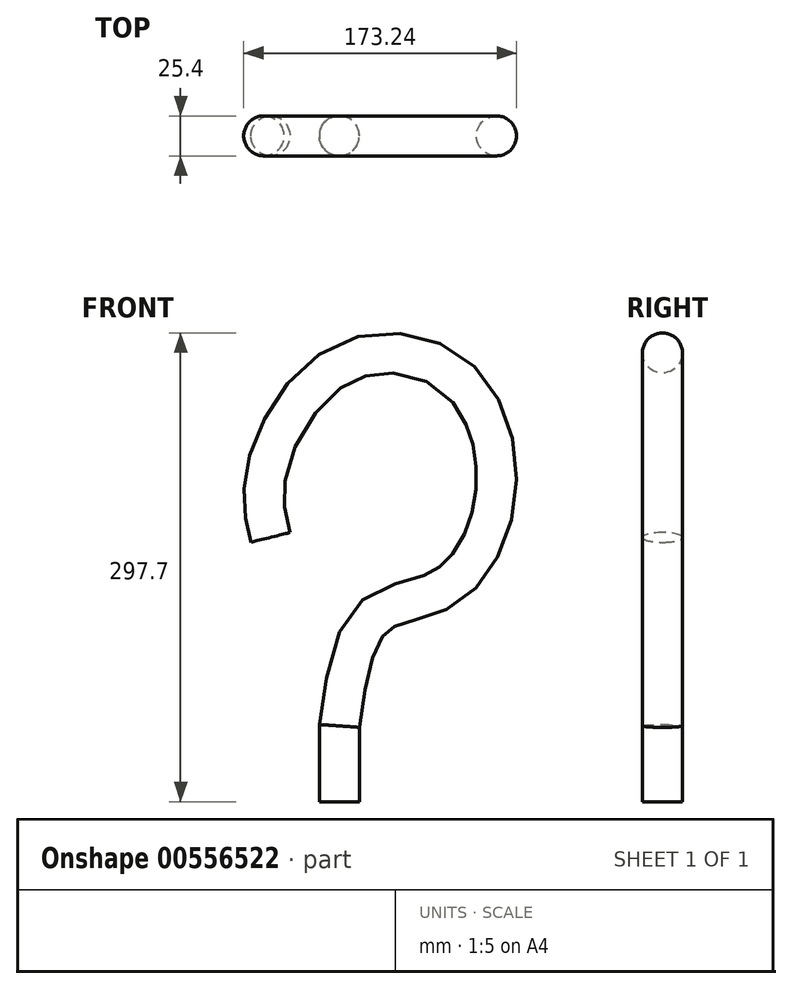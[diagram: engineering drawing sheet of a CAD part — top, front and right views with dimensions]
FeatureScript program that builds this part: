
annotation { "Feature Type Name" : "Feature", "Feature Type Description" : "" }
export const myFeature = defineFeature(function(context is Context, id is Id, definition is map)
    precondition{}
    {
        {
            var Q0;
            Q0=qCreatedBy(makeId("Top.planeOp"),FACE);
            var sketch = newSketch(context, id + "F0", { "sketchPlane" : qUnion([Q0])});
            skCircle(sketch, "E0", {"center": v(0, 0) * mm, "radius": 12.7 * mm});
            skSolve(sketch);
        }
        {
            var Q0;
            Q0=qCreatedBy(makeId("Front.planeOp"),FACE);
            var sketch = newSketch(context, id + "F1", { "sketchPlane" : qUnion([Q0])});
            skLineSegment(sketch, "E1", {"start": v(0, 0) * mm, "end": v(0, 48.1) * mm});
            skFitSpline(sketch, "E2", {"points": [v(0, 48.1) * mm, v(22.17, 117.86) * mm, v(66.5, 135.7) * mm, v(99.3, 195.57) * mm, v(73.38, 270.45) * mm, v(0, 277.22) * mm, v(-46.66, 208.5) * mm, v(-43.75, 167.83) * mm], "startDerivative": vector(79.12, 571.17) * mm, "endDerivative": vector(80.97, -324.05) * mm});
            skSolve(sketch);
        }
        {
            var Q0;
            Q0 = qSketchRegion(id + "F0", true);
            var Q1;
            Q1 = qConstructionFilter(qBodyType(qCreatedBy(id + "F1" ,EDGE), BodyType.WIRE), ConstructionObject.NO);
            sweep(context, id + "F2", {"profiles" : qUnion([Q0]), "path" : qUnion([Q1])});
        }
    });
